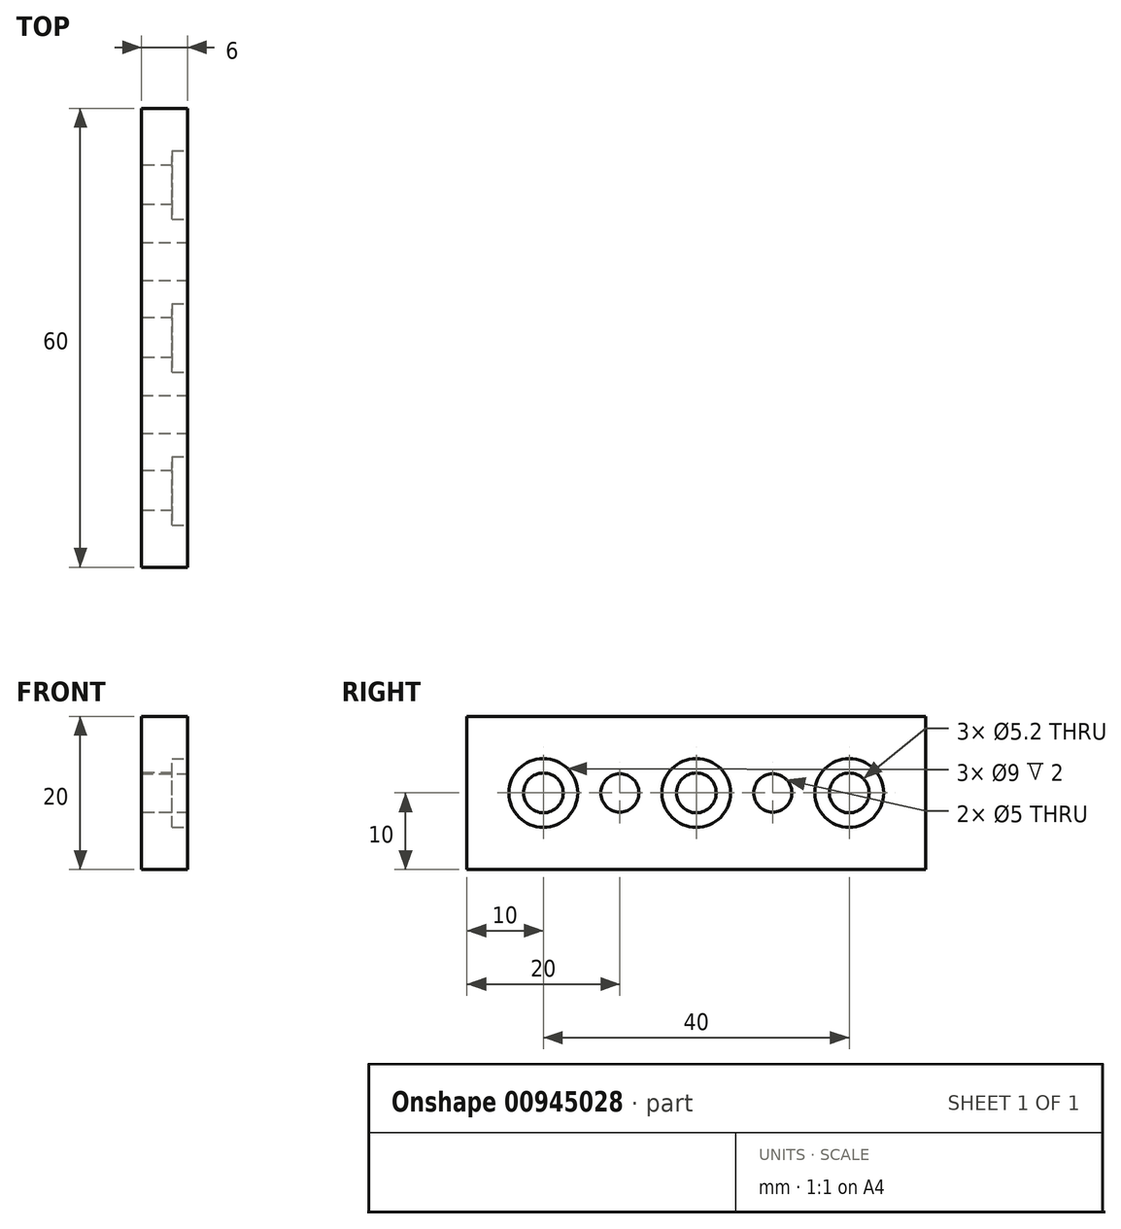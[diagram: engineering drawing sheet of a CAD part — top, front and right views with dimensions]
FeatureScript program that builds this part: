
annotation { "Feature Type Name" : "Feature", "Feature Type Description" : "" }
export const myFeature = defineFeature(function(context is Context, id is Id, definition is map)
    precondition{}
    {
        {
            var Q0;
            Q0=qCreatedBy(makeId("Right.planeOp"),FACE);
            var sketch = newSketch(context, id + "F0", { "sketchPlane" : qUnion([Q0])});
            skLineSegment(sketch, "E0.bottom", {"start": v(30, -10) * mm, "end": v(-30, -10) * mm});
            skLineSegment(sketch, "E0.top", {"start": v(30, 10) * mm, "end": v(-30, 10) * mm});
            skLineSegment(sketch, "E0.left", {"start": v(30, -10) * mm, "end": v(30, 10) * mm});
            skLineSegment(sketch, "E0.right", {"start": v(-30, -10) * mm, "end": v(-30, 10) * mm});
            skPoint(sketch, "E0.middle", {"position": v(0, 0) * mm});
            skCircle(sketch, "E1", {"center": v(-20, 0) * mm, "radius": 2.6 * mm});
            skCircle(sketch, "E2", {"center": v(20, 0) * mm, "radius": 2.6 * mm});
            skCircle(sketch, "E3", {"center": v(0, 0) * mm, "radius": 2.6 * mm});
            skSolve(sketch);
        }
        {
            var Q0;
            Q0=makeQuery(id+"F0.imprint","IMPRINT",FACE,{"disambiguationData":[TD([[makeQuery(id+"F0.imprint","IMPRINT",EDGE,{"derivedFrom":sQuery(id+"F0.wireOp",EDGE,"E0.bottom")}),-1.0]])]});
            extrude(context, id + "F1", {"entities" : qUnion([Q0]), "depth" : 6 * mm});
        }
        {
            var Q0;
            Q0=makeQuery(id+"F1.opExtrude","CAP_FACE",FACE,{"disambiguationData":[OSD([sQuery(id+"F0.wireOp",EDGE,"E0.bottom"),sQuery(id+"F0.wireOp",EDGE,"E0.top"),sQuery(id+"F0.wireOp",EDGE,"E0.left"),sQuery(id+"F0.wireOp",EDGE,"E0.right"),sQuery(id+"F0.wireOp",EDGE,"E1"),sQuery(id+"F0.wireOp",EDGE,"E2"),sQuery(id+"F0.wireOp",EDGE,"E3")])],"isStart":false});
            var sketch = newSketch(context, id + "F2", { "sketchPlane" : qUnion([Q0])});
            skCircle(sketch, "E4", {"center": v(-20, 0) * mm, "radius": 4.5 * mm});
            skCircle(sketch, "E5", {"center": v(0, 0) * mm, "radius": 4.5 * mm});
            skCircle(sketch, "E6", {"center": v(20, 0) * mm, "radius": 4.5 * mm});
            skSolve(sketch);
        }
        {
            var Q0;
            Q0=qSketchRegion(id+"F2",true);
            extrude(context, id + "F3", {"entities" : qUnion([Q0]), "operationType" : NewBodyOperationType.REMOVE, "oppositeDirection" : true, "depth" : 2 * mm});
        }
        {
            var Q0;
            Q0=makeQuery(id+"F1.opExtrude","CAP_FACE",FACE,{"disambiguationData":[OSD([sQuery(id+"F0.wireOp",EDGE,"E0.bottom"),sQuery(id+"F0.wireOp",EDGE,"E0.top"),sQuery(id+"F0.wireOp",EDGE,"E0.left"),sQuery(id+"F0.wireOp",EDGE,"E0.right"),sQuery(id+"F0.wireOp",EDGE,"E1"),sQuery(id+"F0.wireOp",EDGE,"E2"),sQuery(id+"F0.wireOp",EDGE,"E3")])],"isStart":false});
            var sketch = newSketch(context, id + "F4", { "sketchPlane" : qUnion([Q0])});
            skCircle(sketch, "E7", {"center": v(-10, 0) * mm, "radius": 2.5 * mm});
            skCircle(sketch, "E8", {"center": v(10, 0) * mm, "radius": 2.5 * mm});
            skSolve(sketch);
        }
        {
            var Q0;
            Q0=qSketchRegion(id+"F4",true);
            extrude(context, id + "F5", {"entities" : qUnion([Q0]), "operationType" : NewBodyOperationType.REMOVE, "oppositeDirection" : true, "depth" : 25 * mm});
        }
    });
